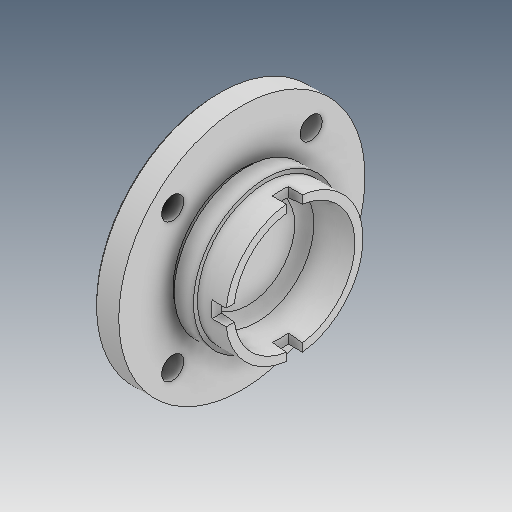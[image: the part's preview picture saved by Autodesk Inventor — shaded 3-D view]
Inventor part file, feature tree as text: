
AUTODESK INVENTOR PART (.ipt)
format: ipt  version: 2025 (Build 290162000, 162)  size: 402,944 bytes
history: native  units: in
note: dims shown in document units (in); Inventor stores cm internally (conversion verified against a paired STEP export)
features: sketch x5, extrude x3, revolve x1, chamfer x1, fillet x1
ambient origin geometry x8: Origin, YZ Plane, XZ Plane, XY Plane, X Axis, Y Axis, Z Axis, Center Point
bodies: 实体1 (feature_tree)
feature tree (11):
  revolve  "旋转1"  [1 undecoded]
  extrude  "拉伸1"  Depth=0.4724in
  extrude  "拉伸2"  Depth=1.3386in
  extrude  "拉伸3"  Depth=0.0984in
  chamfer  "倒角1"  Angle=45.0deg  [1 undecoded]
  fillet  "圆角1"  Radius=0.0394in
  sketch  "草图1"  dims[d3=0.3937in d0=0.4331in d1=1.0236in d2=2.4016in]
  sketch  "草图2"  dims[d6=1.4173in d7=1.3386in]
  sketch  "草图3"  dims[d8=0.4724in d9=0.0984in]
  sketch  "草图4"  dims[d10=1.3386in d11=45.0deg d12=0.0394in d13=0.5906in d14=1.1811in d15=0.5792in d16=90.0deg d17=0.2756in d18=0.315in d19=0.0in d20=0.2756in d21=0.315in d22=0.0in d23=0.4331in d24=1.9094in d25=1.5748in d27=360.0deg d29=0.315in d30=0.0in d31=0.0394in d32=0.0787in d33=45.0deg d34=0.1969in d35=45.0deg]
  sketch  "草图 - 环形阵列1"  dims[d4=1.0236in d5=0.4724in]
note: 2 required parameter values undecoded (feature->parameter linkage not recoverable at this tier; creation-order binding heuristic only, values carry confidence <= 0.55)